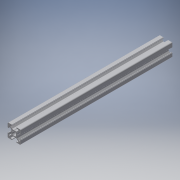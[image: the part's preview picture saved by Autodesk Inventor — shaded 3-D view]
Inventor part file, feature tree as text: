
AUTODESK INVENTOR PART (.ipt)
format: ipt  version: 2016 (Build 200138000, 138)  size: 395,776 bytes
history: native  units: in
note: dims shown in document units (in); Inventor stores cm internally (conversion verified against a paired STEP export)
features: other x5, sketch x1
ambient origin geometry x8: Origin, YZ Plane, XZ Plane, XY Plane, X Axis, Y Axis, Z Axis, Center Point
bodies: Solid1 (feature_tree)
feature tree (6):
  other  "Bosch 20x20 9 in actual.ipt"
  other  "Blocks"
  other  "20x20"
  other  "Solid1::Bosch 20x20 9 in actual.ipt"
  other  "TaggingFeature1"
  sketch  "Sketch1"  dims[d0=0.3937in]
